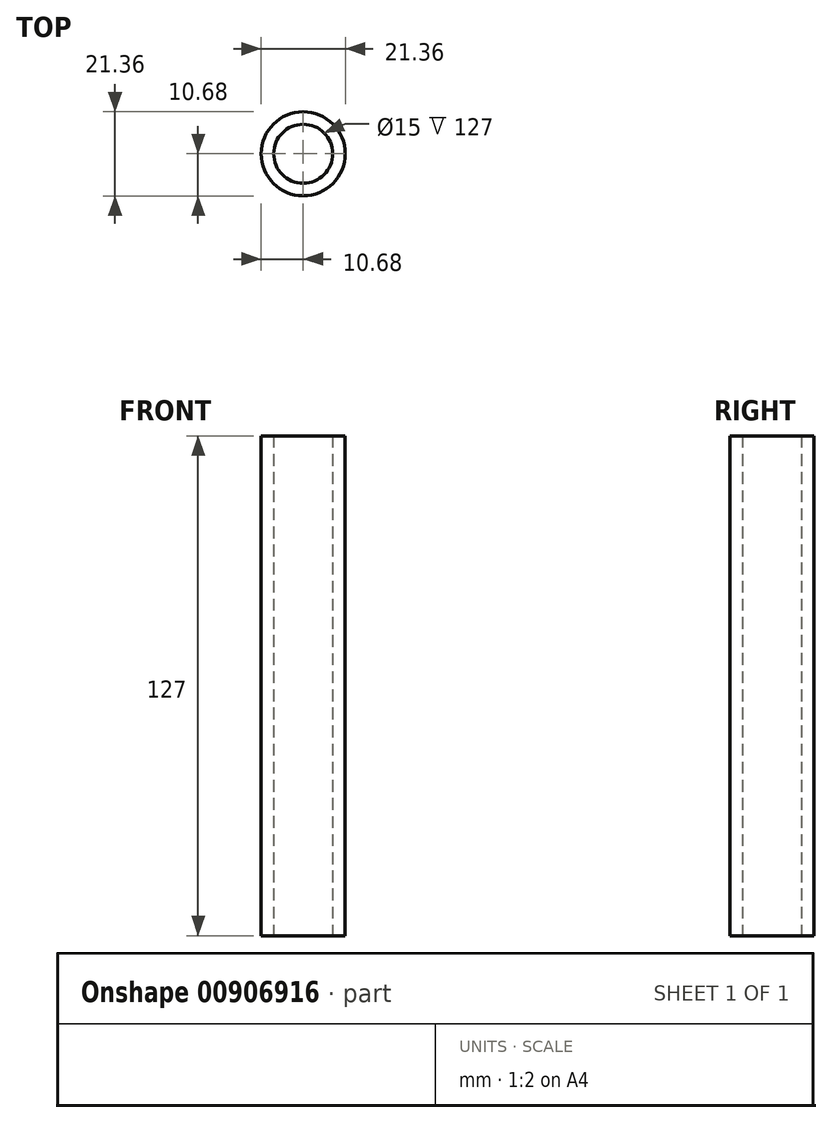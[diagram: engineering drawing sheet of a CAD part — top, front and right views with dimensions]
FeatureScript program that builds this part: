
annotation { "Feature Type Name" : "Feature", "Feature Type Description" : "" }
export const myFeature = defineFeature(function(context is Context, id is Id, definition is map)
    precondition{}
    {
        {
            var Q0;
            Q0=qCreatedBy(makeId("Top.planeOp"),FACE);
            var sketch = newSketch(context, id + "F0", { "sketchPlane" : qUnion([Q0])});
            skCircle(sketch, "E0", {"center": v(0, 0) * mm, "radius": 7.5 * mm});
            skCircle(sketch, "E1", {"center": v(0, 0) * mm, "radius": 10.68 * mm});
            skSolve(sketch);
        }
        {
            var Q0;
            Q0=makeQuery(id+"F0.imprint","IMPRINT",FACE,{"disambiguationData":[TD([[makeQuery(id+"F0.imprint","IMPRINT",EDGE,{"derivedFrom":sQuery(id+"F0.wireOp",EDGE,"E0")}),-1.0]])]});
            extrude(context, id + "F1", {"entities" : qUnion([Q0]), "depth" : 127 * mm, "offsetDistance" : 25.4 * mm});
        }
    });
